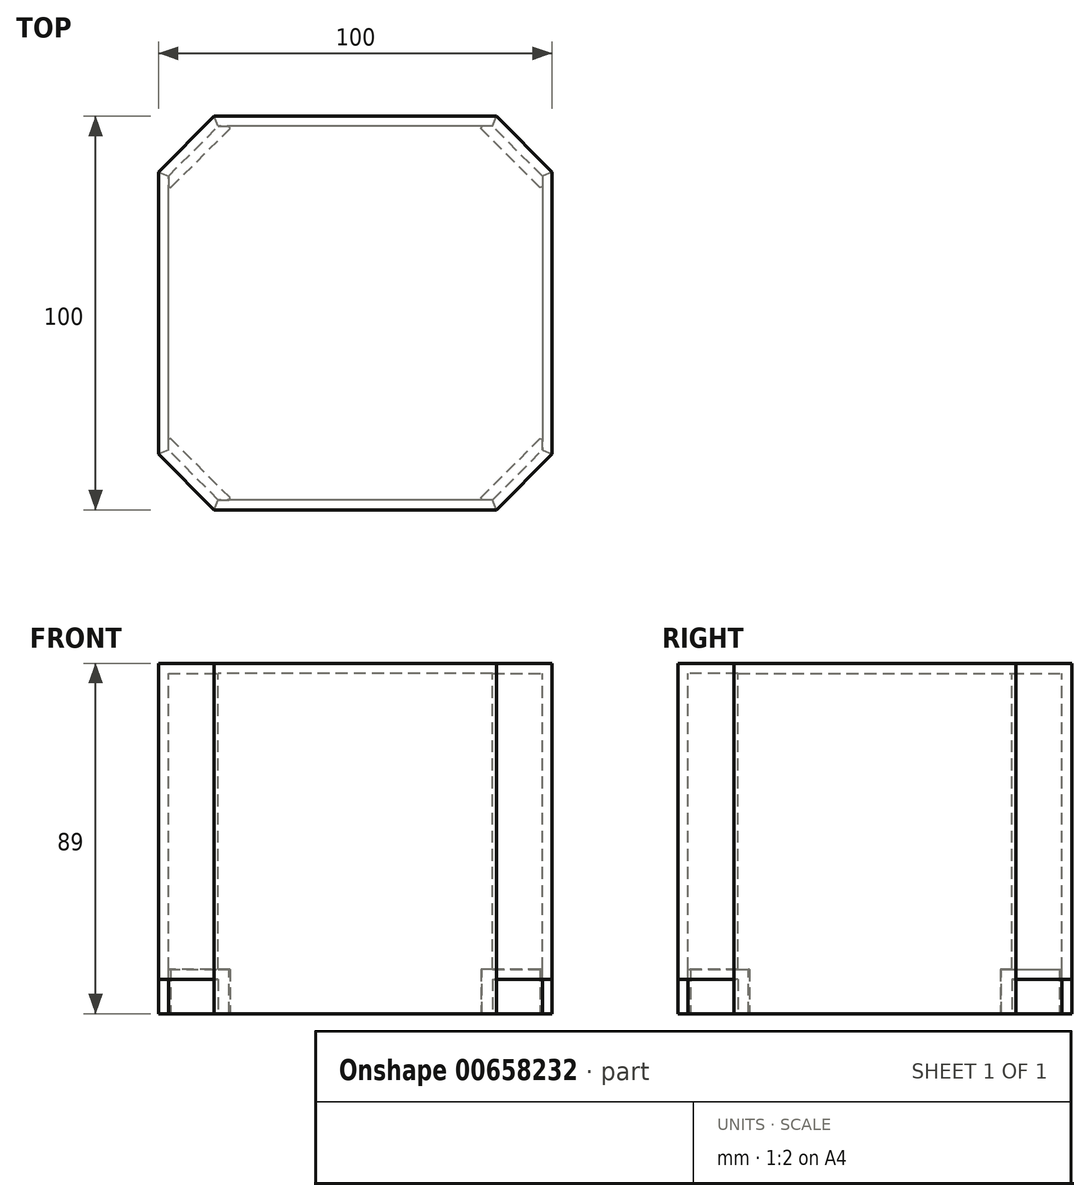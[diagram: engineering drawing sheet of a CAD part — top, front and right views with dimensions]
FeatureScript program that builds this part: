
annotation { "Feature Type Name" : "Feature", "Feature Type Description" : "" }
export const myFeature = defineFeature(function(context is Context, id is Id, definition is map)
    precondition{}
    {
        {
            var Q0;
            Q0=qCreatedBy(makeId("Top.planeOp"),FACE);
            var sketch = newSketch(context, id + "F0", { "sketchPlane" : qUnion([Q0])});
            skLineSegment(sketch, "E0.top", {"start": v(35.86, 50) * mm, "end": v(-35.86, 50) * mm});
            skLineSegment(sketch, "E0.right", {"start": v(-50, -35.86) * mm, "end": v(-50, 35.86) * mm});
            skPoint(sketch, "E0.middle", {"position": v(0, 0) * mm});
            skLineSegment(sketch, "E1", {"start": v(50, 35.86) * mm, "end": v(50, -35.86) * mm});
            skLineSegment(sketch, "E2", {"start": v(35.86, -50) * mm, "end": v(-35.86, -50) * mm});
            skPoint(sketch, "E3.orphan", {"position": v(50, -50) * mm});
            skPoint(sketch, "E4.orphan", {"position": v(50, 50) * mm});
            skPoint(sketch, "E5.orphan", {"position": v(-50, 50) * mm});
            skPoint(sketch, "E6.orphan", {"position": v(-50, -50) * mm});
            skLineSegment(sketch, "E7", {"start": v(-50, 35.86) * mm, "end": v(-35.86, 50) * mm});
            skLineSegment(sketch, "E8", {"start": v(-50, -35.86) * mm, "end": v(-35.86, -50) * mm});
            skLineSegment(sketch, "E9", {"start": v(35.86, -50) * mm, "end": v(50, -35.86) * mm});
            skLineSegment(sketch, "E10", {"start": v(50, 35.86) * mm, "end": v(35.86, 50) * mm});
            skSolve(sketch);
        }
        {
            var Q0;
            Q0=makeQuery(id+"F0.imprint","IMPRINT",FACE,{"disambiguationData":[TD([[makeQuery(id+"F0.imprint","IMPRINT",EDGE,{"derivedFrom":sQuery(id+"F0.wireOp",EDGE,"E0.top")}),1.0]])]});
            extrude(context, id + "F1", {"entities" : qUnion([Q0]), "oppositeDirection" : true, "depth" : 89 * mm, "offsetDistance" : 25 * mm});
        }
        {
            var Q0;
            Q0=makeQuery(id+"F1.opExtrude","CAP_FACE",FACE,{"disambiguationData":[OSD([sQuery(id+"F0.wireOp",EDGE,"E0.top"),sQuery(id+"F0.wireOp",EDGE,"E0.right"),sQuery(id+"F0.wireOp",EDGE,"E1"),sQuery(id+"F0.wireOp",EDGE,"E2"),sQuery(id+"F0.wireOp",EDGE,"a81161d5-af72-463f-a547-fc9cf6ec181d.trimOffspring"),sQuery(id+"F0.wireOp",EDGE,"b752013c-e330-477a-90bb-637ca92a0956.1.1"),sQuery(id+"F0.wireOp",EDGE,"b752013c-e330-477a-90bb-637ca92a0956.2.1"),sQuery(id+"F0.wireOp",EDGE,"b752013c-e330-477a-90bb-637ca92a0956.3.1"),sQuery(id+"F0.wireOp",EDGE,"E7"),sQuery(id+"F0.wireOp",EDGE,"E8"),sQuery(id+"F0.wireOp",EDGE,"E9"),sQuery(id+"F0.wireOp",EDGE,"E10"),sQuery(id+"F0.wireOp",EDGE,"df3f3f33-884c-45b5-baa6-508adabc5ac8.0"),sQuery(id+"F0.wireOp",EDGE,"b6195fe1-1faf-4117-bf94-b5b96006fe31.0"),sQuery(id+"F0.wireOp",EDGE,"13665105-d05f-45cb-afe6-ec81d838e7ea.0"),sQuery(id+"F0.wireOp",EDGE,"31c45408-af9b-49ba-bf27-6d656661cca3.0")])],"isStart":false});
            var sketch = newSketch(context, id + "F2", { "sketchPlane" : qUnion([Q0])});
            skLineSegment(sketch, "E11", {"start": v(-47.5, 34.82) * mm, "end": v(-50, 35.86) * mm});
            skLineSegment(sketch, "E12", {"start": v(-50, 35.86) * mm, "end": v(-35.86, 50) * mm});
            skLineSegment(sketch, "E13", {"start": v(-35.86, 50) * mm, "end": v(-34.82, 47.5) * mm});
            skLineSegment(sketch, "E14", {"start": v(-34.82, 47.5) * mm, "end": v(-47.5, 34.82) * mm});
            skLineSegment(sketch, "E15", {"start": v(-34.82, -47.5) * mm, "end": v(-35.86, -50) * mm});
            skLineSegment(sketch, "E16", {"start": v(-35.86, -50) * mm, "end": v(-50, -35.86) * mm});
            skLineSegment(sketch, "E17", {"start": v(-50, -35.86) * mm, "end": v(-47.5, -34.82) * mm});
            skLineSegment(sketch, "E18", {"start": v(-47.5, -34.82) * mm, "end": v(-34.82, -47.5) * mm});
            skLineSegment(sketch, "E19", {"start": v(34.82, -47.5) * mm, "end": v(35.86, -50) * mm});
            skLineSegment(sketch, "E20", {"start": v(35.86, -50) * mm, "end": v(50, -35.86) * mm});
            skLineSegment(sketch, "E21", {"start": v(50, -35.86) * mm, "end": v(47.5, -34.82) * mm});
            skLineSegment(sketch, "E22", {"start": v(47.5, -34.82) * mm, "end": v(34.82, -47.5) * mm});
            skLineSegment(sketch, "E23", {"start": v(35.86, 50) * mm, "end": v(34.82, 47.5) * mm});
            skLineSegment(sketch, "E24", {"start": v(34.82, 47.5) * mm, "end": v(47.5, 34.82) * mm});
            skLineSegment(sketch, "E25", {"start": v(47.5, 34.82) * mm, "end": v(50, 35.86) * mm});
            skLineSegment(sketch, "E26", {"start": v(50, 35.86) * mm, "end": v(35.86, 50) * mm});
            skSolve(sketch);
        }
        {
            var Q0;
            Q0=makeQuery(id+"F2.imprint","IMPRINT",FACE,{"disambiguationData":[TD([[makeQuery(id+"F2.imprint","IMPRINT",EDGE,{"derivedFrom":sQuery(id+"F2.wireOp",EDGE,"E11")}),-1.0]])]});
            var Q1;
            Q1=makeQuery(id+"F2.imprint","IMPRINT",FACE,{"disambiguationData":[TD([[makeQuery(id+"F2.imprint","IMPRINT",EDGE,{"derivedFrom":sQuery(id+"F2.wireOp",EDGE,"E15")}),-1.0]])]});
            var Q2;
            Q2=makeQuery(id+"F2.imprint","IMPRINT",FACE,{"disambiguationData":[TD([[makeQuery(id+"F2.imprint","IMPRINT",EDGE,{"derivedFrom":sQuery(id+"F2.wireOp",EDGE,"E23")}),1.0]])]});
            var Q3;
            Q3=makeQuery(id+"F2.imprint","IMPRINT",FACE,{"disambiguationData":[TD([[makeQuery(id+"F2.imprint","IMPRINT",EDGE,{"derivedFrom":sQuery(id+"F2.wireOp",EDGE,"E19")}),1.0]])]});
            extrude(context, id + "F3", {"entities" : qUnion([Q0, Q1, Q2, Q3]), "operationType" : NewBodyOperationType.REMOVE, "oppositeDirection" : true, "depth" : 8.75 * mm, "offsetDistance" : 25 * mm});
        }
        {
            var Q0;
            Q0=makeQuery(id+"F1.opExtrude","CAP_FACE",FACE,{"disambiguationData":[OSD([sQuery(id+"F0.wireOp",EDGE,"E0.top"),sQuery(id+"F0.wireOp",EDGE,"E0.right"),sQuery(id+"F0.wireOp",EDGE,"E1"),sQuery(id+"F0.wireOp",EDGE,"E2"),sQuery(id+"F0.wireOp",EDGE,"E7"),sQuery(id+"F0.wireOp",EDGE,"E8"),sQuery(id+"F0.wireOp",EDGE,"E9"),sQuery(id+"F0.wireOp",EDGE,"E10")])],"isStart":false});
            shell(context, id + "F4", {"entities" : qUnion([Q0]), "thickness" : 2.5 * mm});
        }
    });
